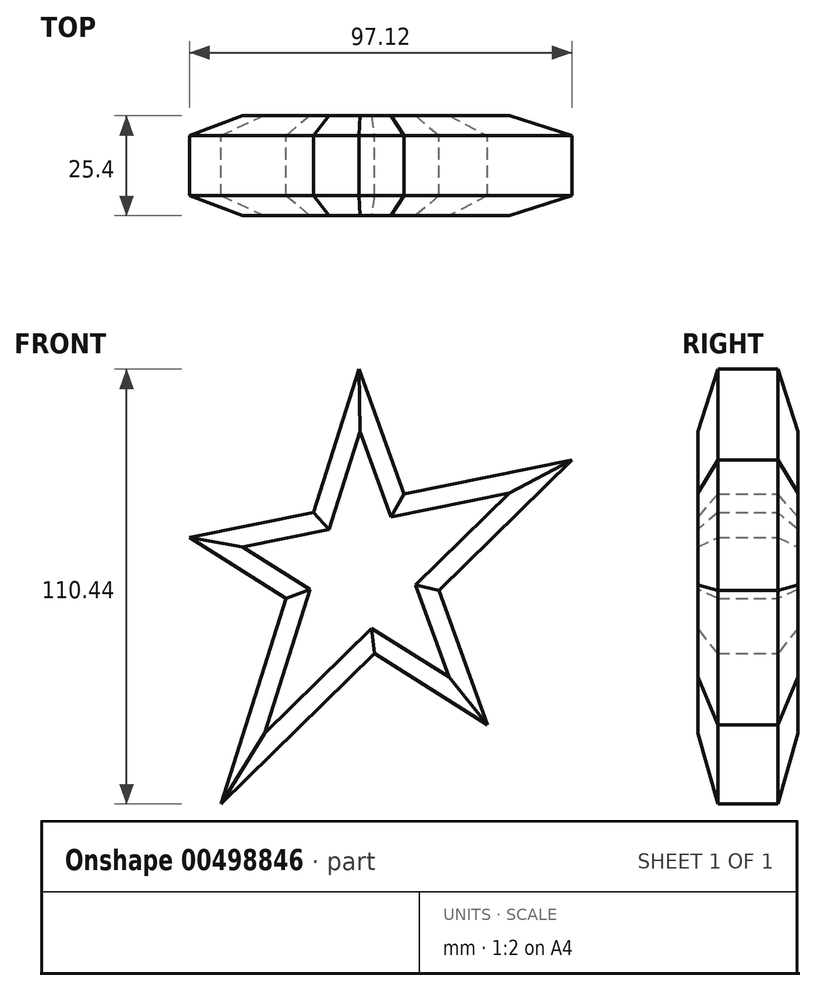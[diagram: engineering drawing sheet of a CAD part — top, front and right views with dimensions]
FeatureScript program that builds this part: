
annotation { "Feature Type Name" : "Feature", "Feature Type Description" : "" }
export const myFeature = defineFeature(function(context is Context, id is Id, definition is map)
    precondition{}
    {
        {
            var Q0;
            Q0=qCreatedBy(makeId("Front.planeOp"),FACE);
            var sketch = newSketch(context, id + "F0", { "sketchPlane" : qUnion([Q0])});
            skLineSegment(sketch, "E0", {"start": v(32.64, -33.87) * mm, "end": v(3.91, -15.8) * mm});
            skLineSegment(sketch, "E1", {"start": v(-43.01, 13.7) * mm, "end": v(-11.53, 20.09) * mm});
            skLineSegment(sketch, "E2", {"start": v(54.11, 33.41) * mm, "end": v(20.3, 0.26) * mm});
            skLineSegment(sketch, "E3", {"start": v(-35.02, -53.98) * mm, "end": v(-18.46, -1.74) * mm});
            skLineSegment(sketch, "E4", {"start": v(0, 56.46) * mm, "end": v(11.46, 24.75) * mm});
            skLineSegment(sketch, "E5.trimOffspring", {"start": v(20.3, 0.26) * mm, "end": v(32.64, -33.87) * mm});
            skLineSegment(sketch, "E6.trimOffspring", {"start": v(-11.53, 20.09) * mm, "end": v(0, 56.46) * mm});
            skLineSegment(sketch, "E7.trimOffspring", {"start": v(-18.46, -1.74) * mm, "end": v(-43.01, 13.7) * mm});
            skLineSegment(sketch, "E8.trimOffspring", {"start": v(3.91, -15.8) * mm, "end": v(-35.02, -53.98) * mm});
            skLineSegment(sketch, "E9.trimOffspring", {"start": v(11.46, 24.75) * mm, "end": v(54.11, 33.41) * mm});
            skSolve(sketch);
        }
        {
            var Q0;
            Q0=makeQuery(id+"F0.imprint","IMPRINT",FACE,{"disambiguationData":[TD([[makeQuery(id+"F0.imprint","IMPRINT",EDGE,{"derivedFrom":sQuery(id+"F0.wireOp",EDGE,"E0")}),-1.0]])]});
            extrude(context, id + "F1", {"entities" : qUnion([Q0]), "depth" : 25.4 * mm, "offsetDistance" : 25.4 * mm});
        }
        {
            var Q0;
            Q0=makeQuery(id+"F1.opExtrude","CAP_EDGE",EDGE,{"disambiguationData":[OSD([sQuery(id+"F0.wireOp",EDGE,"E6.trimOffspring")])],"isStart":false});
            var Q1;
            Q1=makeQuery(id+"F1.opExtrude","CAP_EDGE",EDGE,{"disambiguationData":[OSD([sQuery(id+"F0.wireOp",EDGE,"E1")])],"isStart":false});
            var Q2;
            Q2=makeQuery(id+"F1.opExtrude","CAP_FACE",FACE,{"disambiguationData":[OSD([sQuery(id+"F0.wireOp",EDGE,"E0"),sQuery(id+"F0.wireOp",EDGE,"E1"),sQuery(id+"F0.wireOp",EDGE,"E2"),sQuery(id+"F0.wireOp",EDGE,"E3"),sQuery(id+"F0.wireOp",EDGE,"E4"),sQuery(id+"F0.wireOp",EDGE,"E5.trimOffspring"),sQuery(id+"F0.wireOp",EDGE,"E6.trimOffspring"),sQuery(id+"F0.wireOp",EDGE,"E7.trimOffspring"),sQuery(id+"F0.wireOp",EDGE,"E8.trimOffspring"),sQuery(id+"F0.wireOp",EDGE,"E9.trimOffspring")])],"isStart":false});
            chamfer(context, id + "F2", {"entities" : qUnion([Q0, Q1, Q2]), "width" : 5.08 * mm, "tangentPropagation" : true});
        }
        {
            var Q0;
            Q0=makeQuery(id+"F1.opExtrude","CAP_FACE",FACE,{"disambiguationData":[OSD([sQuery(id+"F0.wireOp",EDGE,"E0"),sQuery(id+"F0.wireOp",EDGE,"E1"),sQuery(id+"F0.wireOp",EDGE,"E2"),sQuery(id+"F0.wireOp",EDGE,"E3"),sQuery(id+"F0.wireOp",EDGE,"E4"),sQuery(id+"F0.wireOp",EDGE,"E5.trimOffspring"),sQuery(id+"F0.wireOp",EDGE,"E6.trimOffspring"),sQuery(id+"F0.wireOp",EDGE,"E7.trimOffspring"),sQuery(id+"F0.wireOp",EDGE,"E8.trimOffspring"),sQuery(id+"F0.wireOp",EDGE,"E9.trimOffspring")])],"isStart":true});
            chamfer(context, id + "F3", {"entities" : qUnion([Q0]), "width" : 5.08 * mm, "tangentPropagation" : true});
        }
    });
